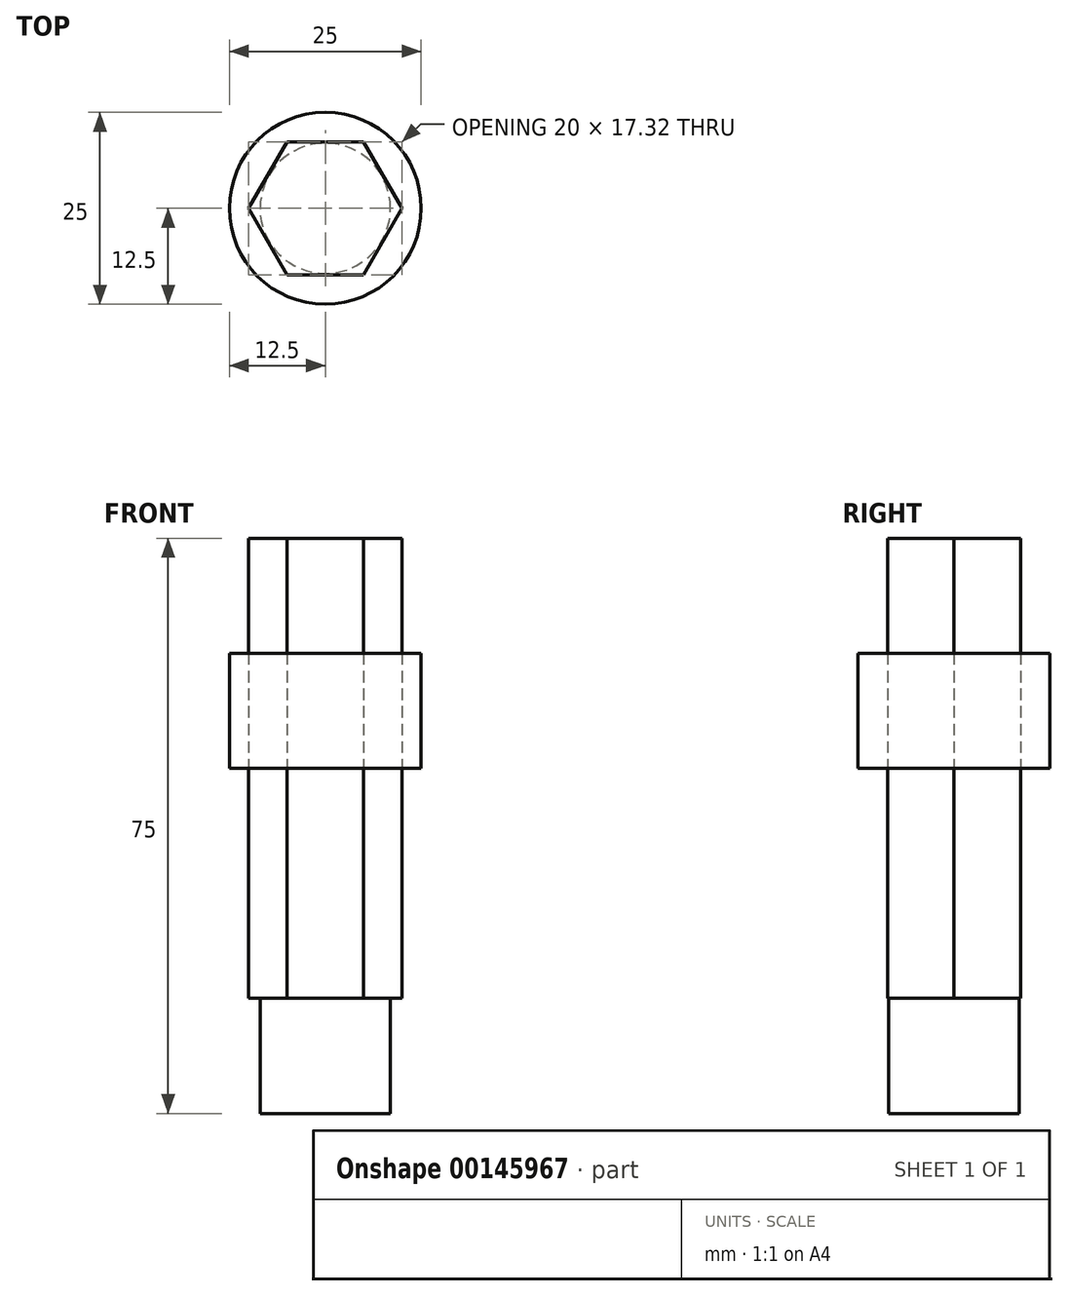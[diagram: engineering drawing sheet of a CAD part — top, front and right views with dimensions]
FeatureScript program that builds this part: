
annotation { "Feature Type Name" : "Feature", "Feature Type Description" : "" }
export const myFeature = defineFeature(function(context is Context, id is Id, definition is map)
    precondition{}
    {
        {
            var Q0;
            Q0=qCreatedBy(makeId("Top.planeOp"),FACE);
            var sketch = newSketch(context, id + "F0", { "sketchPlane" : qUnion([Q0])});
            skCircle(sketch, "E0.cCircle", {"center": v(0, 0) * mm, "radius": 8.66 * mm, "construction": true});
            skLineSegment(sketch, "E0.0", {"start": v(-10, 0) * mm, "end": v(-5, 8.66) * mm});
            skLineSegment(sketch, "E0.1", {"start": v(-5, 8.66) * mm, "end": v(5, 8.66) * mm});
            skLineSegment(sketch, "E0.2", {"start": v(5, 8.66) * mm, "end": v(10, 0) * mm});
            skLineSegment(sketch, "E0.3", {"start": v(10, 0) * mm, "end": v(5, -8.66) * mm});
            skLineSegment(sketch, "E0.4", {"start": v(5, -8.66) * mm, "end": v(-5, -8.66) * mm});
            skLineSegment(sketch, "E0.5", {"start": v(-5, -8.66) * mm, "end": v(-10, 0) * mm});
            skPoint(sketch, "E0.0.midPoint", {"position": v(-7.5, 4.33) * mm});
            skSolve(sketch);
        }
        {
            var Q0;
            Q0=makeQuery(id+"F0.imprint","IMPRINT",FACE,{"disambiguationData":[TD([[makeQuery(id+"F0.imprint","IMPRINT",EDGE,{"derivedFrom":sQuery(id+"F0.wireOp",EDGE,"E0.0")}),-1.0]])]});
            extrude(context, id + "F1", {"entities" : qUnion([Q0]), "depth" : 30 * mm});
        }
        {
            var Q0;
            Q0=makeQuery(id+"F1.opExtrude","CAP_FACE",FACE,{"disambiguationData":[OSD([sQuery(id+"F0.wireOp",EDGE,"E0.0"),sQuery(id+"F0.wireOp",EDGE,"E0.1"),sQuery(id+"F0.wireOp",EDGE,"E0.2"),sQuery(id+"F0.wireOp",EDGE,"E0.3"),sQuery(id+"F0.wireOp",EDGE,"E0.4"),sQuery(id+"F0.wireOp",EDGE,"E0.5")])],"isStart":false});
            var sketch = newSketch(context, id + "F2", { "sketchPlane" : qUnion([Q0])});
            skCircle(sketch, "E1", {"center": v(0, 0) * mm, "radius": 12.5 * mm});
            skSolve(sketch);
        }
        {
            var Q0;
            Q0=makeQuery(id+"F2.imprint","IMPRINT",FACE,{"disambiguationData":[TD([[makeQuery(id+"F2.imprint","IMPRINT",EDGE,{"derivedFrom":sQuery(id+"F2.wireOp",EDGE,"E1")}),1.0]])]});
            extrude(context, id + "F3", {"entities" : qUnion([Q0]), "depth" : 15 * mm});
        }
        {
            var Q0;
            Q0=makeQuery(id+"F1.opExtrude","CAP_FACE",FACE,{"disambiguationData":[OSD([sQuery(id+"F0.wireOp",EDGE,"E0.0"),sQuery(id+"F0.wireOp",EDGE,"E0.1"),sQuery(id+"F0.wireOp",EDGE,"E0.2"),sQuery(id+"F0.wireOp",EDGE,"E0.3"),sQuery(id+"F0.wireOp",EDGE,"E0.4"),sQuery(id+"F0.wireOp",EDGE,"E0.5")])],"isStart":false});
            extrude(context, id + "F4", {"entities" : qUnion([Q0]), "depth" : 30 * mm});
        }
        {
            var Q0;
            Q0=makeQuery(id+"F1.opExtrude","CAP_FACE",FACE,{"disambiguationData":[OSD([sQuery(id+"F0.wireOp",EDGE,"E0.0"),sQuery(id+"F0.wireOp",EDGE,"E0.1"),sQuery(id+"F0.wireOp",EDGE,"E0.2"),sQuery(id+"F0.wireOp",EDGE,"E0.3"),sQuery(id+"F0.wireOp",EDGE,"E0.4"),sQuery(id+"F0.wireOp",EDGE,"E0.5")])],"isStart":true});
            var sketch = newSketch(context, id + "F5", { "sketchPlane" : qUnion([Q0])});
            skCircle(sketch, "E2", {"center": v(0, 0) * mm, "radius": 8.5 * mm});
            skSolve(sketch);
        }
        {
            var Q0;
            Q0=makeQuery(id+"F5.imprint","IMPRINT",FACE,{"disambiguationData":[TD([[makeQuery(id+"F5.imprint","IMPRINT",EDGE,{"derivedFrom":sQuery(id+"F5.wireOp",EDGE,"E2")}),1.0]])]});
            extrude(context, id + "F6", {"entities" : qUnion([Q0]), "operationType" : NewBodyOperationType.ADD, "depth" : 15 * mm});
        }
    });
